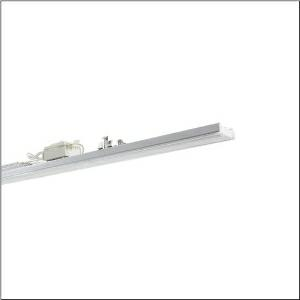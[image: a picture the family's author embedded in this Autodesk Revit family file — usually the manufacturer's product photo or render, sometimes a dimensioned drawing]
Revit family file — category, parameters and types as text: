
# Revit family: licross_r__21_recessed_ho_52tl12dv4l2m_1f59
name_source: partatom
category: Lighting Fixtures
units: mm (PartAtom-declared; Revit-internal decimal feet)

## family parameters
Cut with Voids When Loaded = No
Host = Face
Light Source = No
Part Type = Normal
Room Calculation Point = No
Round Connector Dimension = Use Diameter
Shared = No

## types (1)
- --- (1 x LED, 22710 lm, 125.6 W, 4000K)
    Apparent Load = 126 VA
    CIE Flux Codes = 69 91 98 100 100
    Color Rendering = 80
    Color Temperature = 4000K
    Default Elevation = 1800 mm
    Description = Licross® 21 Recessed HO, luminaire insert, of sheet steel, galvanised, coil coated, white, length: 2.250mm, width: 66mm, height: 67mm, LED rated luminous flux: 22.710lm, light colour: 840, control gear: DALI 2, with plug, 5-pole, with phase selection, mains connection: 220..240V, AC, 50/60Hz, rated input power: 126W, internal wiring halogen-free, primary optical cover: cover, of PMMA, light emission: direct distribution, primary light characteristic: symmetric, protection rating (complete): IP40, insulation class (complete): insulation class I (protective earthing), certification: CE, ENEC, VDE, UKCA, protection symbol: D if used in an environment without relevant dust loads with corresponding accessories, impact resistance: IK06, permissible ambient temperature for indoor applications: -40..+30°C, corresponds to IFS (International Featured Standards) requirements for safety and quality in the food industry, reducing of maximum allowable ambient temperature of 5°C with ceiling mounting, LABS conformity tested according to VDMA 24364:2018-05, packaging unit: 1 piece
    Height = 58 mm
    Lamp = 1 x LED
    Lamp Light Flux = 22710 lm
    Lamp Power = 125.6 W
    Lamp count = 1
    Length = 2250 mm
    Luminous efficacy = 181 lm/W
    Manufacturer = Siteco
    ModVariant = No
    Model = 52TL12DV4L2M
    Mounting Place = Ceiling
    Mounting Type = Pendant
    Number of Poles = 1
    OnlyDefault = Yes
    Power Factor = 1
    Product Name = Licross® 21 Recessed HO
    Product group = luminaire insert | ceiling pendant
    ProductGroupID = 902
    Protection Class = Protection class I
    Protection Degree = IP 40
    RLX_Detail_Level = 1
    RLX_Emergency_Light_Flux = 0 lm
    RLX_Emergency_Type = 0
    RLX_Emergency_Type_DB = No
    RlxData = <blob elided: 29761 chars, md5=c03d2012>
    Socket = socket
    Standby Power = 0 W
    System Light Flux = 22710 lm
    System Power = 126 W
    Type Comments = factory setting: luminous flux: 100 % | dim-lin: 254 | 489 mA
    Type Image = l_1296930.jpg
    URL = http://relux.com
    VarID = @adj_138247
    Voltage = 0 V
    Weight = 0.00 kg
    Width = 66 mm

## geometry (parser evidence)
native form markers: Blend x4, Sweep x9
no freeform markers — native parametric forms only
